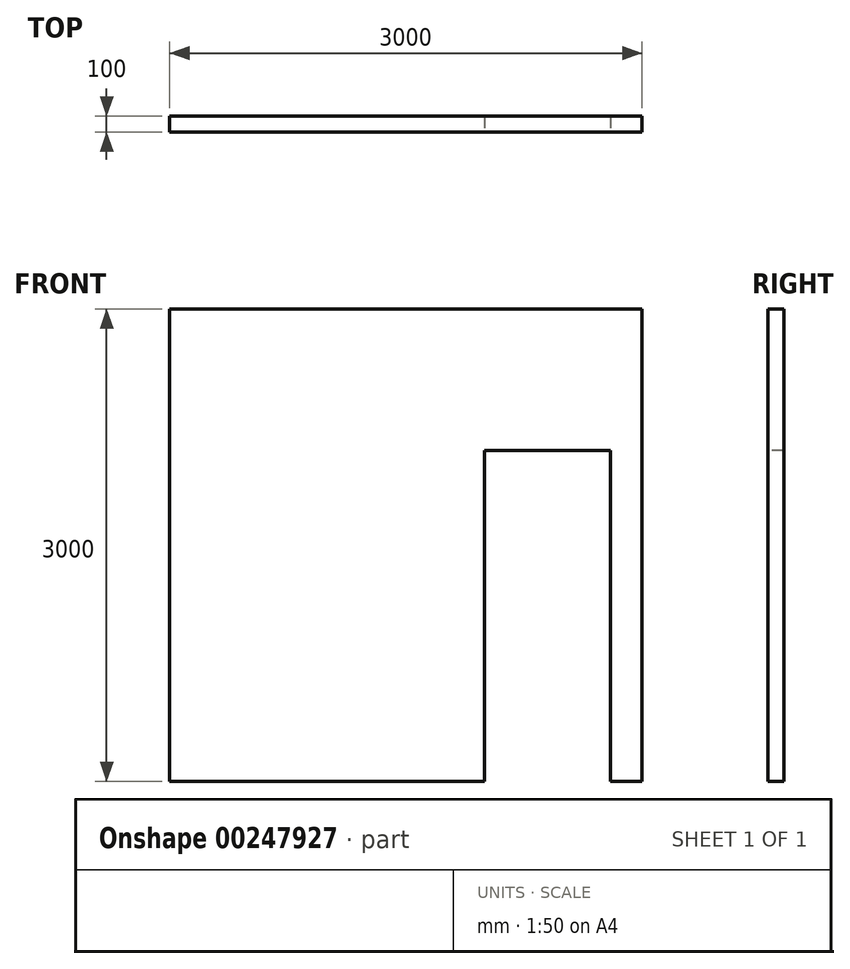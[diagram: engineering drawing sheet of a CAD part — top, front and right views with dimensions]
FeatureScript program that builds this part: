
annotation { "Feature Type Name" : "Feature", "Feature Type Description" : "" }
export const myFeature = defineFeature(function(context is Context, id is Id, definition is map)
    precondition{}
    {
        {
            var Q0;
            Q0=qCreatedBy(makeId("Front.planeOp"),FACE);
            var sketch = newSketch(context, id + "F0", { "sketchPlane" : qUnion([Q0])});
            skLineSegment(sketch, "E0.bottom", {"start": v(1500, 0) * mm, "end": v(-1500, 0) * mm});
            skLineSegment(sketch, "E0.top", {"start": v(1500, 3000) * mm, "end": v(-1500, 3000) * mm});
            skLineSegment(sketch, "E0.left", {"start": v(1500, 0) * mm, "end": v(1500, 3000) * mm});
            skLineSegment(sketch, "E0.right", {"start": v(-1500, 0) * mm, "end": v(-1500, 3000) * mm});
            skPoint(sketch, "E0.middle", {"position": v(0, 1500) * mm});
            skSolve(sketch);
        }
        {
            var Q0;
            Q0=makeQuery(id+"F0.imprint","IMPRINT",FACE,{"disambiguationData":[TD([[makeQuery(id+"F0.imprint","IMPRINT",EDGE,{"derivedFrom":sQuery(id+"F0.wireOp",EDGE,"E0.bottom")}),-1.0]])]});
            extrude(context, id + "F1", {"entities" : qUnion([Q0]), "endBound" : BoundingType.SYMMETRIC, "depth" : 100 * mm});
        }
        {
            var Q0;
            Q0=makeQuery(id+"F1.opExtrude","CAP_FACE",FACE,{"disambiguationData":[OSD([sQuery(id+"F0.wireOp",EDGE,"E0.bottom"),sQuery(id+"F0.wireOp",EDGE,"E0.top"),sQuery(id+"F0.wireOp",EDGE,"E0.left"),sQuery(id+"F0.wireOp",EDGE,"E0.right")])],"isStart":false});
            var sketch = newSketch(context, id + "F2", { "sketchPlane" : qUnion([Q0])});
            skLineSegment(sketch, "E1.bottom", {"start": v(1300, 0) * mm, "end": v(500, 0) * mm});
            skLineSegment(sketch, "E1.top", {"start": v(1300, 2100) * mm, "end": v(500, 2100) * mm});
            skLineSegment(sketch, "E1.left", {"start": v(1300, 0) * mm, "end": v(1300, 2100) * mm});
            skLineSegment(sketch, "E1.right", {"start": v(500, 0) * mm, "end": v(500, 2100) * mm});
            skPoint(sketch, "E1.middle", {"position": v(900, 1050) * mm});
            skLineSegment(sketch, "E2", {"start": v(-1500, 3000) * mm, "end": v(500, 3000) * mm, "construction": true});
            skSolve(sketch);
        }
        {
            var Q0;
            Q0=makeQuery(id+"F2.imprint","IMPRINT",FACE,{"disambiguationData":[TD([[makeQuery(id+"F2.imprint","IMPRINT",EDGE,{"derivedFrom":sQuery(id+"F2.wireOp",EDGE,"E1.bottom")}),-1.0]])]});
            extrude(context, id + "F3", {"entities" : qUnion([Q0]), "operationType" : NewBodyOperationType.REMOVE, "endBound" : BoundingType.THROUGH_ALL, "oppositeDirection" : true, "depth" : 25 * mm});
        }
    });
